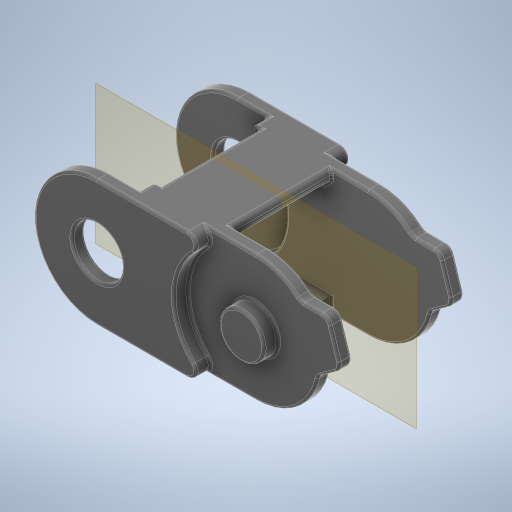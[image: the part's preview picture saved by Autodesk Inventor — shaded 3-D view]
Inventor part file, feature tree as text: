
AUTODESK INVENTOR PART (.ipt)
format: ipt  version: 2024 (Build 280153000, 153)  size: 770,048 bytes
history: native  units: mm
features: extrude x5, fillet x5, sketch x3, projected_geometry x2, chamfer x1, mirror x1
ambient origin geometry x8: Origin, YZ Plane, XZ Plane, XY Plane, X Axis, Y Axis, Z Axis, Center Point
bodies: Solid1 (feature_tree)
feature tree (17):
  sketch  "Sketch1"  dims[d2=14.0mm d3=16.0mm]
  extrude  "Extrusion1"  Depth=16.0mm
  extrude  "Extrusion2"  Depth=36.0mm
  sketch  "Sketch2"  dims[d4=10.0mm d6=36.0mm]
  extrude  "Extrusion3"  Depth=17.0mm TaperAngle=0.0deg
  extrude  "Extrusion4"  Depth=11.0mm TaperAngle=0.0deg
  fillet  "Fillet1"  Radius=8.0mm
  sketch  "Sketch3"  dims[d8=8.0mm d9=17.0mm d10=0.0mm d11=11.0mm d12=0.0mm d13=8.0mm d14=5.0mm d15=5.5mm d16=0.5mm d17=0.0mm d18=0.0mm d19=1.6mm d20=0.0mm d21=1.0mm d22=1.0mm d23=2.0mm d24=45.0deg d25=1.6mm d26=0.0mm d27=0.5mm d28=1.0mm d30=0.5mm d31=0.25mm d32=18.804993mm d35=18.804993mm]
  chamfer  "Chamfer1"  Distance=5.0mm
  extrude  "Extrusion5"  Depth=5.5mm
  fillet  "Fillet2"  Radius=0.5mm
  mirror  "Mirror1"
  fillet  "Fillet3"  [1 undecoded]
  fillet  "Fillet5"  Radius=1.6mm
  fillet  "Fillet6"  Radius=1.0mm
  projected_geometry  "Projected Loop1"
  projected_geometry  "Projected Loop2"
note: 1 required parameter value undecoded (feature->parameter linkage not recoverable at this tier; creation-order binding heuristic only, values carry confidence <= 0.55)
